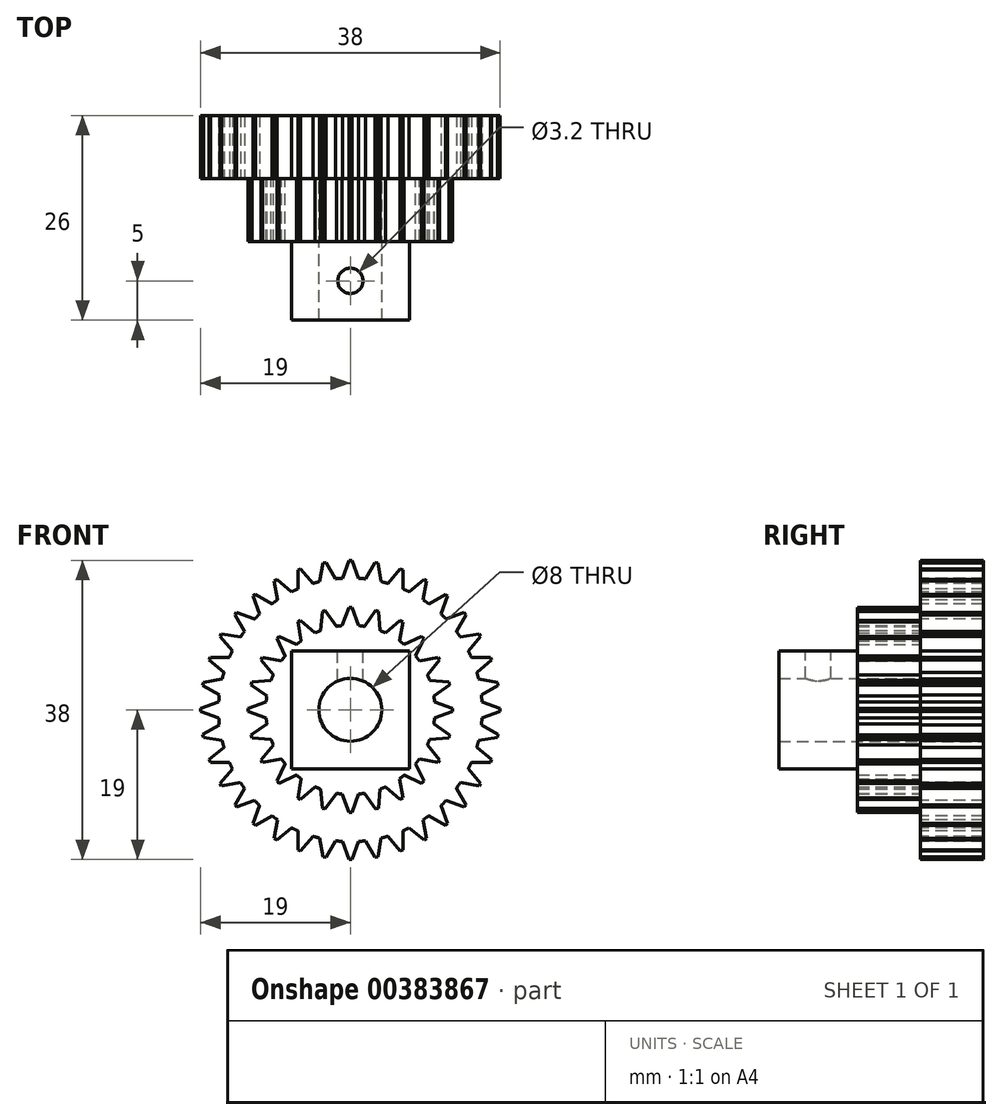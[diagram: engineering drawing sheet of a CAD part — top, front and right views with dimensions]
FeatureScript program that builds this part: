
annotation { "Feature Type Name" : "Feature", "Feature Type Description" : "" }
export const myFeature = defineFeature(function(context is Context, id is Id, definition is map)
    precondition{}
    {
        {
            var Q0;
            Q0=qCreatedBy(makeId("Front.planeOp"),FACE);
            var sketch = newSketch(context, id + "F0", { "sketchPlane" : qUnion([Q0])});
            skCircle(sketch, "E0", {"center": v(0, 0) * mm, "radius": 4 * mm});
            skCircle(sketch, "E1", {"center": v(0, 0) * mm, "radius": 10.75 * mm});
            skCircle(sketch, "E2", {"center": v(0, 0) * mm, "radius": 13 * mm, "construction": true});
            skLineSegment(sketch, "E3", {"start": v(-1.02, 10.7) * mm, "end": v(-0.19, 13) * mm});
            skLineSegment(sketch, "E4", {"start": v(-0.19, 13) * mm, "end": v(0, 13) * mm});
            skLineSegment(sketch, "E5", {"start": v(-1.02, 10.7) * mm, "end": v(-1.02, 13.91) * mm, "construction": true});
            skLineSegment(sketch, "E6.MirrorCS", {"start": v(0.19, 13) * mm, "end": v(0, 13) * mm});
            skLineSegment(sketch, "E7.MirrorCS", {"start": v(1.02, 10.7) * mm, "end": v(0.19, 13) * mm});
            skLineSegment(sketch, "E8.1.0", {"start": v(-3.76, 10.07) * mm, "end": v(-3.55, 12.5) * mm});
            skLineSegment(sketch, "E8.1.1", {"start": v(-3.55, 12.5) * mm, "end": v(-3.36, 12.56) * mm});
            skLineSegment(sketch, "E8.1.2", {"start": v(-3.18, 12.6) * mm, "end": v(-3.36, 12.56) * mm});
            skLineSegment(sketch, "E8.1.3", {"start": v(-1.78, 10.6) * mm, "end": v(-3.18, 12.6) * mm});
            skLineSegment(sketch, "E8.2.0", {"start": v(-6.24, 8.76) * mm, "end": v(-6.66, 11.16) * mm});
            skLineSegment(sketch, "E8.2.1", {"start": v(-6.66, 11.16) * mm, "end": v(-6.5, 11.26) * mm});
            skLineSegment(sketch, "E8.2.2", {"start": v(-6.34, 11.35) * mm, "end": v(-6.5, 11.26) * mm});
            skLineSegment(sketch, "E8.2.3", {"start": v(-4.46, 9.78) * mm, "end": v(-6.34, 11.35) * mm});
            skLineSegment(sketch, "E8.3.0", {"start": v(-8.3, 6.84) * mm, "end": v(-9.32, 9.06) * mm});
            skLineSegment(sketch, "E8.3.1", {"start": v(-9.32, 9.06) * mm, "end": v(-9.2, 9.2) * mm});
            skLineSegment(sketch, "E8.3.2", {"start": v(-9.06, 9.32) * mm, "end": v(-9.2, 9.2) * mm});
            skLineSegment(sketch, "E8.3.3", {"start": v(-6.84, 8.3) * mm, "end": v(-9.06, 9.32) * mm});
            skLineSegment(sketch, "E8.4.0", {"start": v(-9.78, 4.46) * mm, "end": v(-11.35, 6.34) * mm});
            skLineSegment(sketch, "E8.4.1", {"start": v(-11.35, 6.34) * mm, "end": v(-11.26, 6.5) * mm});
            skLineSegment(sketch, "E8.4.2", {"start": v(-11.16, 6.66) * mm, "end": v(-11.26, 6.5) * mm});
            skLineSegment(sketch, "E8.4.3", {"start": v(-8.76, 6.24) * mm, "end": v(-11.16, 6.66) * mm});
            skLineSegment(sketch, "E8.5.0", {"start": v(-10.6, 1.78) * mm, "end": v(-12.6, 3.18) * mm});
            skLineSegment(sketch, "E8.5.1", {"start": v(-12.6, 3.18) * mm, "end": v(-12.56, 3.36) * mm});
            skLineSegment(sketch, "E8.5.2", {"start": v(-12.5, 3.55) * mm, "end": v(-12.56, 3.36) * mm});
            skLineSegment(sketch, "E8.5.3", {"start": v(-10.07, 3.76) * mm, "end": v(-12.5, 3.55) * mm});
            skLineSegment(sketch, "E8.6.0", {"start": v(-10.7, -1.02) * mm, "end": v(-13, -0.19) * mm});
            skLineSegment(sketch, "E8.6.1", {"start": v(-13, -0.19) * mm, "end": v(-13, 0) * mm});
            skLineSegment(sketch, "E8.6.2", {"start": v(-13, 0.19) * mm, "end": v(-13, 0) * mm});
            skLineSegment(sketch, "E8.6.3", {"start": v(-10.7, 1.02) * mm, "end": v(-13, 0.19) * mm});
            skLineSegment(sketch, "E8.7.0", {"start": v(-10.07, -3.76) * mm, "end": v(-12.5, -3.55) * mm});
            skLineSegment(sketch, "E8.7.1", {"start": v(-12.5, -3.55) * mm, "end": v(-12.56, -3.36) * mm});
            skLineSegment(sketch, "E8.7.2", {"start": v(-12.6, -3.18) * mm, "end": v(-12.56, -3.36) * mm});
            skLineSegment(sketch, "E8.7.3", {"start": v(-10.6, -1.78) * mm, "end": v(-12.6, -3.18) * mm});
            skLineSegment(sketch, "E8.8.0", {"start": v(-8.76, -6.24) * mm, "end": v(-11.16, -6.66) * mm});
            skLineSegment(sketch, "E8.8.1", {"start": v(-11.16, -6.66) * mm, "end": v(-11.26, -6.5) * mm});
            skLineSegment(sketch, "E8.8.2", {"start": v(-11.35, -6.34) * mm, "end": v(-11.26, -6.5) * mm});
            skLineSegment(sketch, "E8.8.3", {"start": v(-9.78, -4.46) * mm, "end": v(-11.35, -6.34) * mm});
            skLineSegment(sketch, "E8.9.0", {"start": v(-6.84, -8.3) * mm, "end": v(-9.06, -9.32) * mm});
            skLineSegment(sketch, "E8.9.1", {"start": v(-9.06, -9.32) * mm, "end": v(-9.2, -9.2) * mm});
            skLineSegment(sketch, "E8.9.2", {"start": v(-9.32, -9.06) * mm, "end": v(-9.2, -9.2) * mm});
            skLineSegment(sketch, "E8.9.3", {"start": v(-8.3, -6.84) * mm, "end": v(-9.32, -9.06) * mm});
            skLineSegment(sketch, "E8.10.0", {"start": v(-4.46, -9.78) * mm, "end": v(-6.34, -11.35) * mm});
            skLineSegment(sketch, "E8.10.1", {"start": v(-6.34, -11.35) * mm, "end": v(-6.5, -11.26) * mm});
            skLineSegment(sketch, "E8.10.2", {"start": v(-6.66, -11.16) * mm, "end": v(-6.5, -11.26) * mm});
            skLineSegment(sketch, "E8.10.3", {"start": v(-6.24, -8.76) * mm, "end": v(-6.66, -11.16) * mm});
            skLineSegment(sketch, "E8.11.0", {"start": v(-1.78, -10.6) * mm, "end": v(-3.18, -12.6) * mm});
            skLineSegment(sketch, "E8.11.1", {"start": v(-3.18, -12.6) * mm, "end": v(-3.36, -12.56) * mm});
            skLineSegment(sketch, "E8.11.2", {"start": v(-3.55, -12.5) * mm, "end": v(-3.36, -12.56) * mm});
            skLineSegment(sketch, "E8.11.3", {"start": v(-3.76, -10.07) * mm, "end": v(-3.55, -12.5) * mm});
            skLineSegment(sketch, "E9.1.12.0", {"start": v(1.02, -10.7) * mm, "end": v(0.19, -13) * mm});
            skLineSegment(sketch, "E9.3.12.0", {"start": v(0.19, -13) * mm, "end": v(0, -13) * mm});
            skLineSegment(sketch, "E9.6.12.0", {"start": v(-0.19, -13) * mm, "end": v(0, -13) * mm});
            skLineSegment(sketch, "E9.9.12.0", {"start": v(-1.02, -10.7) * mm, "end": v(-0.19, -13) * mm});
            skLineSegment(sketch, "E9.1.13.0", {"start": v(3.76, -10.07) * mm, "end": v(3.55, -12.5) * mm});
            skLineSegment(sketch, "E9.3.13.0", {"start": v(3.55, -12.5) * mm, "end": v(3.36, -12.56) * mm});
            skLineSegment(sketch, "E9.6.13.0", {"start": v(3.18, -12.6) * mm, "end": v(3.36, -12.56) * mm});
            skLineSegment(sketch, "E9.9.13.0", {"start": v(1.78, -10.6) * mm, "end": v(3.18, -12.6) * mm});
            skLineSegment(sketch, "E9.1.14.0", {"start": v(6.24, -8.76) * mm, "end": v(6.66, -11.16) * mm});
            skLineSegment(sketch, "E9.3.14.0", {"start": v(6.66, -11.16) * mm, "end": v(6.5, -11.26) * mm});
            skLineSegment(sketch, "E9.6.14.0", {"start": v(6.34, -11.35) * mm, "end": v(6.5, -11.26) * mm});
            skLineSegment(sketch, "E9.9.14.0", {"start": v(4.46, -9.78) * mm, "end": v(6.34, -11.35) * mm});
            skLineSegment(sketch, "E9.1.15.0", {"start": v(8.3, -6.84) * mm, "end": v(9.32, -9.06) * mm});
            skLineSegment(sketch, "E9.3.15.0", {"start": v(9.32, -9.06) * mm, "end": v(9.2, -9.2) * mm});
            skLineSegment(sketch, "E9.6.15.0", {"start": v(9.06, -9.32) * mm, "end": v(9.2, -9.2) * mm});
            skLineSegment(sketch, "E9.9.15.0", {"start": v(6.84, -8.3) * mm, "end": v(9.06, -9.32) * mm});
            skLineSegment(sketch, "E9.1.16.0", {"start": v(9.78, -4.46) * mm, "end": v(11.35, -6.34) * mm});
            skLineSegment(sketch, "E9.3.16.0", {"start": v(11.35, -6.34) * mm, "end": v(11.26, -6.5) * mm});
            skLineSegment(sketch, "E9.6.16.0", {"start": v(11.16, -6.66) * mm, "end": v(11.26, -6.5) * mm});
            skLineSegment(sketch, "E9.9.16.0", {"start": v(8.76, -6.24) * mm, "end": v(11.16, -6.66) * mm});
            skLineSegment(sketch, "E9.1.17.0", {"start": v(10.6, -1.78) * mm, "end": v(12.6, -3.18) * mm});
            skLineSegment(sketch, "E9.3.17.0", {"start": v(12.6, -3.18) * mm, "end": v(12.56, -3.36) * mm});
            skLineSegment(sketch, "E9.6.17.0", {"start": v(12.5, -3.55) * mm, "end": v(12.56, -3.36) * mm});
            skLineSegment(sketch, "E9.9.17.0", {"start": v(10.07, -3.76) * mm, "end": v(12.5, -3.55) * mm});
            skLineSegment(sketch, "E9.1.18.0", {"start": v(10.7, 1.02) * mm, "end": v(13, 0.19) * mm});
            skLineSegment(sketch, "E9.3.18.0", {"start": v(13, 0.19) * mm, "end": v(13, 0) * mm});
            skLineSegment(sketch, "E9.6.18.0", {"start": v(13, -0.19) * mm, "end": v(13, 0) * mm});
            skLineSegment(sketch, "E9.9.18.0", {"start": v(10.7, -1.02) * mm, "end": v(13, -0.19) * mm});
            skLineSegment(sketch, "E9.1.19.0", {"start": v(10.07, 3.76) * mm, "end": v(12.5, 3.55) * mm});
            skLineSegment(sketch, "E9.3.19.0", {"start": v(12.5, 3.55) * mm, "end": v(12.56, 3.36) * mm});
            skLineSegment(sketch, "E9.6.19.0", {"start": v(12.6, 3.18) * mm, "end": v(12.56, 3.36) * mm});
            skLineSegment(sketch, "E9.9.19.0", {"start": v(10.6, 1.78) * mm, "end": v(12.6, 3.18) * mm});
            skLineSegment(sketch, "E9.1.20.0", {"start": v(8.76, 6.24) * mm, "end": v(11.16, 6.66) * mm});
            skLineSegment(sketch, "E9.3.20.0", {"start": v(11.16, 6.66) * mm, "end": v(11.26, 6.5) * mm});
            skLineSegment(sketch, "E9.6.20.0", {"start": v(11.35, 6.34) * mm, "end": v(11.26, 6.5) * mm});
            skLineSegment(sketch, "E9.9.20.0", {"start": v(9.78, 4.46) * mm, "end": v(11.35, 6.34) * mm});
            skLineSegment(sketch, "E9.1.21.0", {"start": v(6.84, 8.3) * mm, "end": v(9.06, 9.32) * mm});
            skLineSegment(sketch, "E9.3.21.0", {"start": v(9.06, 9.32) * mm, "end": v(9.2, 9.2) * mm});
            skLineSegment(sketch, "E9.6.21.0", {"start": v(9.32, 9.06) * mm, "end": v(9.2, 9.2) * mm});
            skLineSegment(sketch, "E9.9.21.0", {"start": v(8.3, 6.84) * mm, "end": v(9.32, 9.06) * mm});
            skLineSegment(sketch, "E9.1.22.0", {"start": v(4.46, 9.78) * mm, "end": v(6.34, 11.35) * mm});
            skLineSegment(sketch, "E9.3.22.0", {"start": v(6.34, 11.35) * mm, "end": v(6.5, 11.26) * mm});
            skLineSegment(sketch, "E9.6.22.0", {"start": v(6.66, 11.16) * mm, "end": v(6.5, 11.26) * mm});
            skLineSegment(sketch, "E9.9.22.0", {"start": v(6.24, 8.76) * mm, "end": v(6.66, 11.16) * mm});
            skLineSegment(sketch, "E9.1.23.0", {"start": v(1.78, 10.6) * mm, "end": v(3.18, 12.6) * mm});
            skLineSegment(sketch, "E9.3.23.0", {"start": v(3.18, 12.6) * mm, "end": v(3.36, 12.56) * mm});
            skLineSegment(sketch, "E9.6.23.0", {"start": v(3.55, 12.5) * mm, "end": v(3.36, 12.56) * mm});
            skLineSegment(sketch, "E9.9.23.0", {"start": v(3.76, 10.07) * mm, "end": v(3.55, 12.5) * mm});
            skSolve(sketch);
        }
        {
            var Q0;
            Q0 = qSketchRegion(id + "F0", true);
            extrude(context, id + "F1", {"entities" : qUnion([Q0]), "depth" : 8 * mm});
        }
        {
            var Q0;
            Q0=qCreatedBy(makeId("Front.planeOp"),FACE);
            var sketch = newSketch(context, id + "F2", { "sketchPlane" : qUnion([Q0])});
            skCircle(sketch, "E10", {"center": v(0, 0) * mm, "radius": 4 * mm});
            skCircle(sketch, "E11", {"center": v(0, 0) * mm, "radius": 16.75 * mm});
            skCircle(sketch, "E12", {"center": v(0, 0) * mm, "radius": 19 * mm, "construction": true});
            skLineSegment(sketch, "E13", {"start": v(-1.02, 16.72) * mm, "end": v(-0.19, 19) * mm});
            skLineSegment(sketch, "E14", {"start": v(-0.19, 19) * mm, "end": v(0, 19) * mm});
            skLineSegment(sketch, "E15", {"start": v(-1.02, 16.72) * mm, "end": v(-1.02, 25.53) * mm, "construction": true});
            skLineSegment(sketch, "E16.MirrorCS", {"start": v(0.19, 19) * mm, "end": v(0, 19) * mm});
            skLineSegment(sketch, "E17.MirrorCS", {"start": v(1.02, 16.72) * mm, "end": v(0.19, 19) * mm});
            skLineSegment(sketch, "E18.1.0", {"start": v(-3.9, 16.29) * mm, "end": v(-3.48, 18.68) * mm});
            skLineSegment(sketch, "E18.1.1", {"start": v(-3.11, 18.74) * mm, "end": v(-3.3, 18.71) * mm});
            skLineSegment(sketch, "E18.1.2", {"start": v(-3.48, 18.68) * mm, "end": v(-3.3, 18.71) * mm});
            skLineSegment(sketch, "E18.1.3", {"start": v(-1.9, 16.64) * mm, "end": v(-3.11, 18.74) * mm});
            skLineSegment(sketch, "E18.2.0", {"start": v(-6.67, 15.36) * mm, "end": v(-6.67, 17.8) * mm});
            skLineSegment(sketch, "E18.2.1", {"start": v(-6.32, 17.92) * mm, "end": v(-6.5, 17.85) * mm});
            skLineSegment(sketch, "E18.2.2", {"start": v(-6.67, 17.8) * mm, "end": v(-6.5, 17.85) * mm});
            skLineSegment(sketch, "E18.2.3", {"start": v(-4.76, 16.06) * mm, "end": v(-6.32, 17.92) * mm});
            skLineSegment(sketch, "E18.3.0", {"start": v(-9.24, 13.97) * mm, "end": v(-9.66, 16.36) * mm});
            skLineSegment(sketch, "E18.3.1", {"start": v(-9.34, 16.55) * mm, "end": v(-9.5, 16.45) * mm});
            skLineSegment(sketch, "E18.3.2", {"start": v(-9.66, 16.36) * mm, "end": v(-9.5, 16.45) * mm});
            skLineSegment(sketch, "E18.3.3", {"start": v(-7.48, 14.99) * mm, "end": v(-9.34, 16.55) * mm});
            skLineSegment(sketch, "E18.4.0", {"start": v(-11.53, 12.15) * mm, "end": v(-12.36, 14.43) * mm});
            skLineSegment(sketch, "E18.4.1", {"start": v(-12.07, 14.68) * mm, "end": v(-12.21, 14.55) * mm});
            skLineSegment(sketch, "E18.4.2", {"start": v(-12.36, 14.43) * mm, "end": v(-12.21, 14.55) * mm});
            skLineSegment(sketch, "E18.4.3", {"start": v(-9.97, 13.46) * mm, "end": v(-12.07, 14.68) * mm});
            skLineSegment(sketch, "E18.5.0", {"start": v(-13.46, 9.97) * mm, "end": v(-14.68, 12.07) * mm});
            skLineSegment(sketch, "E18.5.1", {"start": v(-14.43, 12.36) * mm, "end": v(-14.55, 12.21) * mm});
            skLineSegment(sketch, "E18.5.2", {"start": v(-14.68, 12.07) * mm, "end": v(-14.55, 12.21) * mm});
            skLineSegment(sketch, "E18.5.3", {"start": v(-12.15, 11.53) * mm, "end": v(-14.43, 12.36) * mm});
            skLineSegment(sketch, "E18.6.0", {"start": v(-14.99, 7.48) * mm, "end": v(-16.55, 9.34) * mm});
            skLineSegment(sketch, "E18.6.1", {"start": v(-16.36, 9.66) * mm, "end": v(-16.45, 9.5) * mm});
            skLineSegment(sketch, "E18.6.2", {"start": v(-16.55, 9.34) * mm, "end": v(-16.45, 9.5) * mm});
            skLineSegment(sketch, "E18.6.3", {"start": v(-13.97, 9.24) * mm, "end": v(-16.36, 9.66) * mm});
            skLineSegment(sketch, "E18.7.0", {"start": v(-16.06, 4.76) * mm, "end": v(-17.92, 6.32) * mm});
            skLineSegment(sketch, "E18.7.1", {"start": v(-17.8, 6.67) * mm, "end": v(-17.85, 6.5) * mm});
            skLineSegment(sketch, "E18.7.2", {"start": v(-17.92, 6.32) * mm, "end": v(-17.85, 6.5) * mm});
            skLineSegment(sketch, "E18.7.3", {"start": v(-15.36, 6.67) * mm, "end": v(-17.8, 6.67) * mm});
            skLineSegment(sketch, "E18.8.0", {"start": v(-16.64, 1.9) * mm, "end": v(-18.74, 3.11) * mm});
            skLineSegment(sketch, "E18.8.1", {"start": v(-18.68, 3.48) * mm, "end": v(-18.71, 3.3) * mm});
            skLineSegment(sketch, "E18.8.2", {"start": v(-18.74, 3.11) * mm, "end": v(-18.71, 3.3) * mm});
            skLineSegment(sketch, "E18.8.3", {"start": v(-16.29, 3.9) * mm, "end": v(-18.68, 3.48) * mm});
            skLineSegment(sketch, "E18.9.0", {"start": v(-16.72, -1.02) * mm, "end": v(-19, -0.19) * mm});
            skLineSegment(sketch, "E18.9.1", {"start": v(-19, 0.19) * mm, "end": v(-19, 0) * mm});
            skLineSegment(sketch, "E18.9.2", {"start": v(-19, -0.19) * mm, "end": v(-19, 0) * mm});
            skLineSegment(sketch, "E18.9.3", {"start": v(-16.72, 1.02) * mm, "end": v(-19, 0.19) * mm});
            skLineSegment(sketch, "E18.10.0", {"start": v(-16.29, -3.9) * mm, "end": v(-18.68, -3.48) * mm});
            skLineSegment(sketch, "E18.10.1", {"start": v(-18.74, -3.11) * mm, "end": v(-18.71, -3.3) * mm});
            skLineSegment(sketch, "E18.10.2", {"start": v(-18.68, -3.48) * mm, "end": v(-18.71, -3.3) * mm});
            skLineSegment(sketch, "E18.10.3", {"start": v(-16.64, -1.9) * mm, "end": v(-18.74, -3.11) * mm});
            skLineSegment(sketch, "E18.11.0", {"start": v(-15.36, -6.67) * mm, "end": v(-17.8, -6.67) * mm});
            skLineSegment(sketch, "E18.11.1", {"start": v(-17.92, -6.32) * mm, "end": v(-17.85, -6.5) * mm});
            skLineSegment(sketch, "E18.11.2", {"start": v(-17.8, -6.67) * mm, "end": v(-17.85, -6.5) * mm});
            skLineSegment(sketch, "E18.11.3", {"start": v(-16.06, -4.76) * mm, "end": v(-17.92, -6.32) * mm});
            skLineSegment(sketch, "E18.12.0", {"start": v(-13.97, -9.24) * mm, "end": v(-16.36, -9.66) * mm});
            skLineSegment(sketch, "E18.12.1", {"start": v(-16.55, -9.34) * mm, "end": v(-16.45, -9.5) * mm});
            skLineSegment(sketch, "E18.12.2", {"start": v(-16.36, -9.66) * mm, "end": v(-16.45, -9.5) * mm});
            skLineSegment(sketch, "E18.12.3", {"start": v(-14.99, -7.48) * mm, "end": v(-16.55, -9.34) * mm});
            skLineSegment(sketch, "E18.13.0", {"start": v(-12.15, -11.53) * mm, "end": v(-14.43, -12.36) * mm});
            skLineSegment(sketch, "E18.13.1", {"start": v(-14.68, -12.07) * mm, "end": v(-14.55, -12.21) * mm});
            skLineSegment(sketch, "E18.13.2", {"start": v(-14.43, -12.36) * mm, "end": v(-14.55, -12.21) * mm});
            skLineSegment(sketch, "E18.13.3", {"start": v(-13.46, -9.97) * mm, "end": v(-14.68, -12.07) * mm});
            skLineSegment(sketch, "E18.14.0", {"start": v(-9.97, -13.46) * mm, "end": v(-12.07, -14.68) * mm});
            skLineSegment(sketch, "E18.14.1", {"start": v(-12.36, -14.43) * mm, "end": v(-12.21, -14.55) * mm});
            skLineSegment(sketch, "E18.14.2", {"start": v(-12.07, -14.68) * mm, "end": v(-12.21, -14.55) * mm});
            skLineSegment(sketch, "E18.14.3", {"start": v(-11.53, -12.15) * mm, "end": v(-12.36, -14.43) * mm});
            skLineSegment(sketch, "E18.15.0", {"start": v(-7.48, -14.99) * mm, "end": v(-9.34, -16.55) * mm});
            skLineSegment(sketch, "E18.15.1", {"start": v(-9.66, -16.36) * mm, "end": v(-9.5, -16.45) * mm});
            skLineSegment(sketch, "E18.15.2", {"start": v(-9.34, -16.55) * mm, "end": v(-9.5, -16.45) * mm});
            skLineSegment(sketch, "E18.15.3", {"start": v(-9.24, -13.97) * mm, "end": v(-9.66, -16.36) * mm});
            skLineSegment(sketch, "E18.16.0", {"start": v(-4.76, -16.06) * mm, "end": v(-6.32, -17.92) * mm});
            skLineSegment(sketch, "E18.16.1", {"start": v(-6.67, -17.8) * mm, "end": v(-6.5, -17.85) * mm});
            skLineSegment(sketch, "E18.16.2", {"start": v(-6.32, -17.92) * mm, "end": v(-6.5, -17.85) * mm});
            skLineSegment(sketch, "E18.16.3", {"start": v(-6.67, -15.36) * mm, "end": v(-6.67, -17.8) * mm});
            skLineSegment(sketch, "E18.17.0", {"start": v(-1.9, -16.64) * mm, "end": v(-3.11, -18.74) * mm});
            skLineSegment(sketch, "E18.17.1", {"start": v(-3.48, -18.68) * mm, "end": v(-3.3, -18.71) * mm});
            skLineSegment(sketch, "E18.17.2", {"start": v(-3.11, -18.74) * mm, "end": v(-3.3, -18.71) * mm});
            skLineSegment(sketch, "E18.17.3", {"start": v(-3.9, -16.29) * mm, "end": v(-3.48, -18.68) * mm});
            skLineSegment(sketch, "E18.18.0", {"start": v(1.02, -16.72) * mm, "end": v(0.19, -19) * mm});
            skLineSegment(sketch, "E18.18.1", {"start": v(-0.19, -19) * mm, "end": v(0, -19) * mm});
            skLineSegment(sketch, "E18.18.2", {"start": v(0.19, -19) * mm, "end": v(0, -19) * mm});
            skLineSegment(sketch, "E18.18.3", {"start": v(-1.02, -16.72) * mm, "end": v(-0.19, -19) * mm});
            skLineSegment(sketch, "E18.19.0", {"start": v(3.9, -16.29) * mm, "end": v(3.48, -18.68) * mm});
            skLineSegment(sketch, "E18.19.1", {"start": v(3.11, -18.74) * mm, "end": v(3.3, -18.71) * mm});
            skLineSegment(sketch, "E18.19.2", {"start": v(3.48, -18.68) * mm, "end": v(3.3, -18.71) * mm});
            skLineSegment(sketch, "E18.19.3", {"start": v(1.9, -16.64) * mm, "end": v(3.11, -18.74) * mm});
            skLineSegment(sketch, "E18.20.0", {"start": v(6.67, -15.36) * mm, "end": v(6.67, -17.8) * mm});
            skLineSegment(sketch, "E18.20.1", {"start": v(6.32, -17.92) * mm, "end": v(6.5, -17.85) * mm});
            skLineSegment(sketch, "E18.20.2", {"start": v(6.67, -17.8) * mm, "end": v(6.5, -17.85) * mm});
            skLineSegment(sketch, "E18.20.3", {"start": v(4.76, -16.06) * mm, "end": v(6.32, -17.92) * mm});
            skLineSegment(sketch, "E18.21.0", {"start": v(9.24, -13.97) * mm, "end": v(9.66, -16.36) * mm});
            skLineSegment(sketch, "E18.21.1", {"start": v(9.34, -16.55) * mm, "end": v(9.5, -16.45) * mm});
            skLineSegment(sketch, "E18.21.2", {"start": v(9.66, -16.36) * mm, "end": v(9.5, -16.45) * mm});
            skLineSegment(sketch, "E18.21.3", {"start": v(7.48, -14.99) * mm, "end": v(9.34, -16.55) * mm});
            skLineSegment(sketch, "E18.22.0", {"start": v(11.53, -12.15) * mm, "end": v(12.36, -14.43) * mm});
            skLineSegment(sketch, "E18.22.1", {"start": v(12.07, -14.68) * mm, "end": v(12.21, -14.55) * mm});
            skLineSegment(sketch, "E18.22.2", {"start": v(12.36, -14.43) * mm, "end": v(12.21, -14.55) * mm});
            skLineSegment(sketch, "E18.22.3", {"start": v(9.97, -13.46) * mm, "end": v(12.07, -14.68) * mm});
            skLineSegment(sketch, "E18.23.0", {"start": v(13.46, -9.97) * mm, "end": v(14.68, -12.07) * mm});
            skLineSegment(sketch, "E18.23.1", {"start": v(14.43, -12.36) * mm, "end": v(14.55, -12.21) * mm});
            skLineSegment(sketch, "E18.23.2", {"start": v(14.68, -12.07) * mm, "end": v(14.55, -12.21) * mm});
            skLineSegment(sketch, "E18.23.3", {"start": v(12.15, -11.53) * mm, "end": v(14.43, -12.36) * mm});
            skLineSegment(sketch, "E18.24.0", {"start": v(14.99, -7.48) * mm, "end": v(16.55, -9.34) * mm});
            skLineSegment(sketch, "E18.24.1", {"start": v(16.36, -9.66) * mm, "end": v(16.45, -9.5) * mm});
            skLineSegment(sketch, "E18.24.2", {"start": v(16.55, -9.34) * mm, "end": v(16.45, -9.5) * mm});
            skLineSegment(sketch, "E18.24.3", {"start": v(13.97, -9.24) * mm, "end": v(16.36, -9.66) * mm});
            skLineSegment(sketch, "E18.25.0", {"start": v(16.06, -4.76) * mm, "end": v(17.92, -6.32) * mm});
            skLineSegment(sketch, "E18.25.1", {"start": v(17.8, -6.67) * mm, "end": v(17.85, -6.5) * mm});
            skLineSegment(sketch, "E18.25.2", {"start": v(17.92, -6.32) * mm, "end": v(17.85, -6.5) * mm});
            skLineSegment(sketch, "E18.25.3", {"start": v(15.36, -6.67) * mm, "end": v(17.8, -6.67) * mm});
            skLineSegment(sketch, "E18.26.0", {"start": v(16.64, -1.9) * mm, "end": v(18.74, -3.11) * mm});
            skLineSegment(sketch, "E18.26.1", {"start": v(18.68, -3.48) * mm, "end": v(18.71, -3.3) * mm});
            skLineSegment(sketch, "E18.26.2", {"start": v(18.74, -3.11) * mm, "end": v(18.71, -3.3) * mm});
            skLineSegment(sketch, "E18.26.3", {"start": v(16.29, -3.9) * mm, "end": v(18.68, -3.48) * mm});
            skLineSegment(sketch, "E18.27.0", {"start": v(16.72, 1.02) * mm, "end": v(19, 0.19) * mm});
            skLineSegment(sketch, "E18.27.1", {"start": v(19, -0.19) * mm, "end": v(19, 0) * mm});
            skLineSegment(sketch, "E18.27.2", {"start": v(19, 0.19) * mm, "end": v(19, 0) * mm});
            skLineSegment(sketch, "E18.27.3", {"start": v(16.72, -1.02) * mm, "end": v(19, -0.19) * mm});
            skLineSegment(sketch, "E18.28.0", {"start": v(16.29, 3.9) * mm, "end": v(18.68, 3.48) * mm});
            skLineSegment(sketch, "E18.28.1", {"start": v(18.74, 3.11) * mm, "end": v(18.71, 3.3) * mm});
            skLineSegment(sketch, "E18.28.2", {"start": v(18.68, 3.48) * mm, "end": v(18.71, 3.3) * mm});
            skLineSegment(sketch, "E18.28.3", {"start": v(16.64, 1.9) * mm, "end": v(18.74, 3.11) * mm});
            skLineSegment(sketch, "E18.29.0", {"start": v(15.36, 6.67) * mm, "end": v(17.8, 6.67) * mm});
            skLineSegment(sketch, "E18.29.1", {"start": v(17.92, 6.32) * mm, "end": v(17.85, 6.5) * mm});
            skLineSegment(sketch, "E18.29.2", {"start": v(17.8, 6.67) * mm, "end": v(17.85, 6.5) * mm});
            skLineSegment(sketch, "E18.29.3", {"start": v(16.06, 4.76) * mm, "end": v(17.92, 6.32) * mm});
            skLineSegment(sketch, "E18.30.0", {"start": v(13.97, 9.24) * mm, "end": v(16.36, 9.66) * mm});
            skLineSegment(sketch, "E18.30.1", {"start": v(16.55, 9.34) * mm, "end": v(16.45, 9.5) * mm});
            skLineSegment(sketch, "E18.30.2", {"start": v(16.36, 9.66) * mm, "end": v(16.45, 9.5) * mm});
            skLineSegment(sketch, "E18.30.3", {"start": v(14.99, 7.48) * mm, "end": v(16.55, 9.34) * mm});
            skLineSegment(sketch, "E18.31.0", {"start": v(12.15, 11.53) * mm, "end": v(14.43, 12.36) * mm});
            skLineSegment(sketch, "E18.31.1", {"start": v(14.68, 12.07) * mm, "end": v(14.55, 12.21) * mm});
            skLineSegment(sketch, "E18.31.2", {"start": v(14.43, 12.36) * mm, "end": v(14.55, 12.21) * mm});
            skLineSegment(sketch, "E18.31.3", {"start": v(13.46, 9.97) * mm, "end": v(14.68, 12.07) * mm});
            skLineSegment(sketch, "E18.32.0", {"start": v(9.97, 13.46) * mm, "end": v(12.07, 14.68) * mm});
            skLineSegment(sketch, "E18.32.1", {"start": v(12.36, 14.43) * mm, "end": v(12.21, 14.55) * mm});
            skLineSegment(sketch, "E18.32.2", {"start": v(12.07, 14.68) * mm, "end": v(12.21, 14.55) * mm});
            skLineSegment(sketch, "E18.32.3", {"start": v(11.53, 12.15) * mm, "end": v(12.36, 14.43) * mm});
            skLineSegment(sketch, "E18.33.0", {"start": v(7.48, 14.99) * mm, "end": v(9.34, 16.55) * mm});
            skLineSegment(sketch, "E18.33.1", {"start": v(9.66, 16.36) * mm, "end": v(9.5, 16.45) * mm});
            skLineSegment(sketch, "E18.33.2", {"start": v(9.34, 16.55) * mm, "end": v(9.5, 16.45) * mm});
            skLineSegment(sketch, "E18.33.3", {"start": v(9.24, 13.97) * mm, "end": v(9.66, 16.36) * mm});
            skLineSegment(sketch, "E18.34.0", {"start": v(4.76, 16.06) * mm, "end": v(6.32, 17.92) * mm});
            skLineSegment(sketch, "E18.34.1", {"start": v(6.67, 17.8) * mm, "end": v(6.5, 17.85) * mm});
            skLineSegment(sketch, "E18.34.2", {"start": v(6.32, 17.92) * mm, "end": v(6.5, 17.85) * mm});
            skLineSegment(sketch, "E18.34.3", {"start": v(6.67, 15.36) * mm, "end": v(6.67, 17.8) * mm});
            skLineSegment(sketch, "E18.35.0", {"start": v(1.9, 16.64) * mm, "end": v(3.11, 18.74) * mm});
            skLineSegment(sketch, "E18.35.1", {"start": v(3.48, 18.68) * mm, "end": v(3.3, 18.71) * mm});
            skLineSegment(sketch, "E18.35.2", {"start": v(3.11, 18.74) * mm, "end": v(3.3, 18.71) * mm});
            skLineSegment(sketch, "E18.35.3", {"start": v(3.9, 16.29) * mm, "end": v(3.48, 18.68) * mm});
            skSolve(sketch);
        }
        {
            var Q0;
            Q0 = qSketchRegion(id + "F2", true);
            extrude(context, id + "F3", {"entities" : qUnion([Q0]), "operationType" : NewBodyOperationType.ADD, "depth" : -8 * mm});
        }
        {
            var Q0;
            Q0=makeQuery(id+"F1.opExtrude","CAP_FACE",FACE,{"disambiguationData":[OSD([sQuery(id+"F0.wireOp",EDGE,"E0"),sQuery(id+"F0.wireOp",EDGE,"E1"),sQuery(id+"F0.wireOp",EDGE,"E3"),sQuery(id+"F0.wireOp",EDGE,"E4"),sQuery(id+"F0.wireOp",EDGE,"E6.MirrorCS"),sQuery(id+"F0.wireOp",EDGE,"E7.MirrorCS"),sQuery(id+"F0.wireOp",EDGE,"E8.1.0"),sQuery(id+"F0.wireOp",EDGE,"E8.1.1"),sQuery(id+"F0.wireOp",EDGE,"E8.1.2"),sQuery(id+"F0.wireOp",EDGE,"E8.1.3"),sQuery(id+"F0.wireOp",EDGE,"E8.2.0"),sQuery(id+"F0.wireOp",EDGE,"E8.2.1"),sQuery(id+"F0.wireOp",EDGE,"E8.2.2"),sQuery(id+"F0.wireOp",EDGE,"E8.2.3"),sQuery(id+"F0.wireOp",EDGE,"E8.3.0"),sQuery(id+"F0.wireOp",EDGE,"E8.3.1"),sQuery(id+"F0.wireOp",EDGE,"E8.3.2"),sQuery(id+"F0.wireOp",EDGE,"E8.3.3"),sQuery(id+"F0.wireOp",EDGE,"E8.4.0"),sQuery(id+"F0.wireOp",EDGE,"E8.4.1"),sQuery(id+"F0.wireOp",EDGE,"E8.4.2"),sQuery(id+"F0.wireOp",EDGE,"E8.4.3"),sQuery(id+"F0.wireOp",EDGE,"E8.5.0"),sQuery(id+"F0.wireOp",EDGE,"E8.5.1"),sQuery(id+"F0.wireOp",EDGE,"E8.5.2"),sQuery(id+"F0.wireOp",EDGE,"E8.5.3"),sQuery(id+"F0.wireOp",EDGE,"E8.6.0"),sQuery(id+"F0.wireOp",EDGE,"E8.6.1"),sQuery(id+"F0.wireOp",EDGE,"E8.6.2"),sQuery(id+"F0.wireOp",EDGE,"E8.6.3"),sQuery(id+"F0.wireOp",EDGE,"E8.7.0"),sQuery(id+"F0.wireOp",EDGE,"E8.7.1"),sQuery(id+"F0.wireOp",EDGE,"E8.7.2"),sQuery(id+"F0.wireOp",EDGE,"E8.7.3"),sQuery(id+"F0.wireOp",EDGE,"E8.8.0"),sQuery(id+"F0.wireOp",EDGE,"E8.8.1"),sQuery(id+"F0.wireOp",EDGE,"E8.8.2"),sQuery(id+"F0.wireOp",EDGE,"E8.8.3"),sQuery(id+"F0.wireOp",EDGE,"E8.9.0"),sQuery(id+"F0.wireOp",EDGE,"E8.9.1"),sQuery(id+"F0.wireOp",EDGE,"E8.9.2"),sQuery(id+"F0.wireOp",EDGE,"E8.9.3"),sQuery(id+"F0.wireOp",EDGE,"E8.10.0"),sQuery(id+"F0.wireOp",EDGE,"E8.10.1"),sQuery(id+"F0.wireOp",EDGE,"E8.10.2"),sQuery(id+"F0.wireOp",EDGE,"E8.10.3"),sQuery(id+"F0.wireOp",EDGE,"E8.11.0"),sQuery(id+"F0.wireOp",EDGE,"E8.11.1"),sQuery(id+"F0.wireOp",EDGE,"E8.11.2"),sQuery(id+"F0.wireOp",EDGE,"E8.11.3")])],"isStart":false});
            var sketch = newSketch(context, id + "F4", { "sketchPlane" : qUnion([Q0])});
            skPoint(sketch, "E19.middle", {"position": v(0, 0) * mm});
            skPoint(sketch, "E19.cornerSnap0", {"position": v(6.54, 8.53) * mm});
            skLineSegment(sketch, "E20.bottom", {"start": v(-7.5, 7.5) * mm, "end": v(7.5, 7.5) * mm});
            skLineSegment(sketch, "E20.top", {"start": v(-7.5, -7.5) * mm, "end": v(7.5, -7.5) * mm});
            skLineSegment(sketch, "E20.left", {"start": v(-7.5, 7.5) * mm, "end": v(-7.5, -7.5) * mm});
            skLineSegment(sketch, "E20.right", {"start": v(7.5, 7.5) * mm, "end": v(7.5, -7.5) * mm});
            skCircle(sketch, "E21", {"center": v(0, 0) * mm, "radius": 4 * mm});
            skSolve(sketch);
        }
        {
            var Q0;
            Q0 = qSketchRegion(id + "F4", true);
            extrude(context, id + "F5", {"entities" : qUnion([Q0]), "operationType" : NewBodyOperationType.ADD, "depth" : 10 * mm});
        }
        {
            var Q0;
            Q0=makeQuery(id+"F5.opExtrude","SWEPT_FACE",FACE,{"disambiguationData":[OSD([sQuery(id+"F4.wireOp",EDGE,"E20.bottom")])]});
            var sketch = newSketch(context, id + "F6", { "sketchPlane" : qUnion([Q0])});
            skLineSegment(sketch, "E22", {"start": v(0, -8) * mm, "end": v(0, -13) * mm, "construction": true});
            skLineSegment(sketch, "E23", {"start": v(0, -13) * mm, "end": v(-7.5, -13) * mm, "construction": true});
            skCircle(sketch, "E24", {"center": v(0, -13) * mm, "radius": 1.6 * mm});
            skSolve(sketch);
        }
        {
            var Q0;
            Q0 = qSketchRegion(id + "F6", true);
            var Q1;
            Q1=makeQuery(id+"F5.boolean.opBoolean","MERGE",FACE,{"derivedFrom":[makeQuery(id+"F3.boolean.opBoolean","MERGE",FACE,{"derivedFrom":[makeQuery(id+"F1.opExtrude","SWEPT_FACE",FACE,{"disambiguationData":[OSD([sQuery(id+"F0.wireOp",EDGE,"E0")])]}),makeQuery(id+"F3.opExtrude","SWEPT_FACE",FACE,{"disambiguationData":[OSD([sQuery(id+"F2.wireOp",EDGE,"E10")])]})]}),makeQuery(id+"F5.opExtrude","SWEPT_FACE",FACE,{"disambiguationData":[OSD([sQuery(id+"F4.wireOp",EDGE,"E21")])]})]});
            extrude(context, id + "F7", {"entities" : qUnion([Q0]), "operationType" : NewBodyOperationType.REMOVE, "endBound" : BoundingType.UP_TO_SURFACE, "oppositeDirection" : true, "endBoundEntityFace" : qUnion([Q1]), "depth" : 25 * mm});
        }
    });
